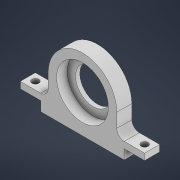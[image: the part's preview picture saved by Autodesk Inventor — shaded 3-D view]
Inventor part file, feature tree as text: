
AUTODESK INVENTOR PART (.ipt)
format: ipt  version: 2021 (Build 250183000, 183)  size: 335,872 bytes
history: native  units: mm
features: extrude x8, sketch x8, fillet x2
ambient origin geometry x8: Origin, YZ Plane, XZ Plane, XY Plane, X Axis, Y Axis, Z Axis, Center Point
bodies: Volumenkörper1 (feature_tree)
feature tree (18):
  extrude  "Extrusion1"  Depth=32.0mm
  sketch  "Skizze2"  dims[d2=24.2mm d3=7.0mm d4=0.0mm d5=6.0mm]
  sketch  "Skizze3"  dims[d6=6.0mm d11=24.2mm]
  extrude  "Extrusion4"  Depth=7.0mm TaperAngle=0.0deg
  fillet  "Rundung1"  Radius=6.0mm
  extrude  "Extrusion6"  Depth=24.2mm
  extrude  "Extrusion7"  Depth=2.0mm TaperAngle=0.0deg
  extrude  "Extrusion8"  Depth=13.0mm TaperAngle=0.0deg
  extrude  "Extrusion9"  Depth=13.0mm
  extrude  "Extrusion10"  Depth=3.5mm
  fillet  "Rundung3"  Radius=3.2mm
  extrude  "Extrusion11"  Depth=3.5mm
  sketch  "Skizze1"  dims[d0=32.0mm d1=32.0mm]
  sketch  "Skizze4"  dims[d12=16.5mm d13=2.0mm d14=0.0mm]
  sketch  "Skizze6"  dims[d15=16.0mm d25=13.0mm d26=0.0mm]
  sketch  "Skizze7"  dims[d27=13.0mm d28=0.0mm d29=3.2mm]
  sketch  "Skizze8"  dims[d30=3.5mm d31=3.5mm d32=3.2mm]
  sketch  "Skizze9"  dims[d33=3.5mm d34=3.5mm d35=10.5mm d36=0.0mm d37=3.5mm d38=0.0mm d39=3.5mm d40=0.0mm d41=3.5mm d42=1.5mm d43=0.0mm]
